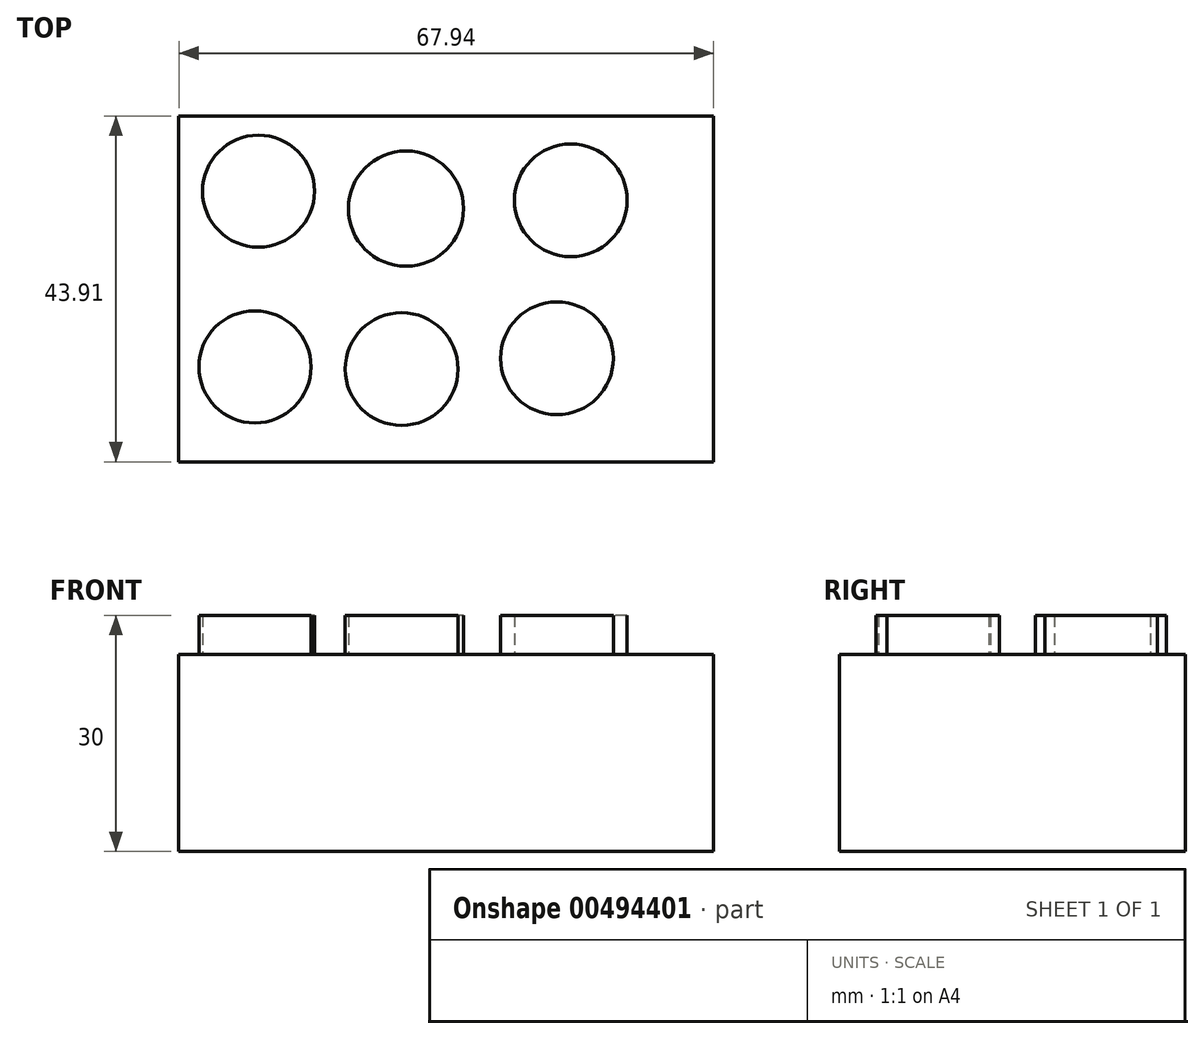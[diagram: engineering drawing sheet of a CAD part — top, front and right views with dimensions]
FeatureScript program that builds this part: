
annotation { "Feature Type Name" : "Feature", "Feature Type Description" : "" }
export const myFeature = defineFeature(function(context is Context, id is Id, definition is map)
    precondition{}
    {
        {
            var Q0;
            Q0=qCreatedBy(makeId("Top.planeOp"),FACE);
            var sketch = newSketch(context, id + "F0", { "sketchPlane" : qUnion([Q0])});
            skLineSegment(sketch, "E0.bottom", {"start": v(-65.61, 41.66) * mm, "end": v(2.33, 41.66) * mm});
            skLineSegment(sketch, "E0.top", {"start": v(-65.61, -2.25) * mm, "end": v(2.33, -2.25) * mm});
            skLineSegment(sketch, "E0.left", {"start": v(-65.61, 41.66) * mm, "end": v(-65.61, -2.25) * mm});
            skLineSegment(sketch, "E0.right", {"start": v(2.33, 41.66) * mm, "end": v(2.33, -2.25) * mm});
            skSolve(sketch);
        }
        {
            var Q0;
            Q0 = qSketchRegion(id + "F0", true);
            extrude(context, id + "F1", {"entities" : qUnion([Q0]), "depth" : 25 * mm});
        }
        {
            var Q0;
            Q0=makeQuery(id+"F1.opExtrude","CAP_FACE",FACE,{"disambiguationData":[OSD([sQuery(id+"F0.wireOp",EDGE,"E0.bottom"),sQuery(id+"F0.wireOp",EDGE,"E0.top"),sQuery(id+"F0.wireOp",EDGE,"E0.left"),sQuery(id+"F0.wireOp",EDGE,"E0.right")])],"isStart":false});
            var sketch = newSketch(context, id + "F2", { "sketchPlane" : qUnion([Q0])});
            skCircle(sketch, "E1", {"center": v(-55.95, 9.8) * mm, "radius": 7.13 * mm});
            skSolve(sketch);
        }
        {
            var Q0;
            Q0=makeQuery(id+"F2.imprint","IMPRINT",FACE,{"disambiguationData":[TD([[makeQuery(id+"F2.imprint","IMPRINT",EDGE,{"derivedFrom":sQuery(id+"F2.wireOp",EDGE,"E1")}),-1.0]])]});
            var sketch = newSketch(context, id + "F3", { "sketchPlane" : qUnion([Q0])});
            skCircle(sketch, "E2", {"center": v(-37.31, 9.53) * mm, "radius": 7.16 * mm});
            skSolve(sketch);
        }
        {
            var Q0;
            Q0=makeQuery(id+"F2.imprint","IMPRINT",FACE,{"disambiguationData":[TD([[makeQuery(id+"F2.imprint","IMPRINT",EDGE,{"derivedFrom":sQuery(id+"F2.wireOp",EDGE,"E1")}),-1.0]])]});
            var sketch = newSketch(context, id + "F4", { "sketchPlane" : qUnion([Q0])});
            skCircle(sketch, "E3", {"center": v(-17.58, 10.9) * mm, "radius": 7.16 * mm});
            skSolve(sketch);
        }
        {
            var Q0;
            Q0 = qSketchRegion(id + "F4", true);
            extrude(context, id + "F5", {"entities" : qUnion([Q0]), "operationType" : NewBodyOperationType.ADD, "depth" : 5 * mm});
        }
        {
            var Q0;
            Q0=makeQuery(id+"F2.imprint","IMPRINT",FACE,{"disambiguationData":[TD([[makeQuery(id+"F2.imprint","IMPRINT",EDGE,{"derivedFrom":sQuery(id+"F2.wireOp",EDGE,"E1")}),1.0]])]});
            extrude(context, id + "F6", {"entities" : qUnion([Q0]), "operationType" : NewBodyOperationType.ADD, "depth" : 5 * mm});
        }
        {
            var Q0;
            Q0 = qSketchRegion(id + "F3", true);
            extrude(context, id + "F7", {"entities" : qUnion([Q0]), "operationType" : NewBodyOperationType.ADD, "depth" : 5 * mm});
        }
        {
            var Q0;
            Q0=makeQuery(id+"F1.opExtrude","CAP_FACE",FACE,{"disambiguationData":[OSD([sQuery(id+"F0.wireOp",EDGE,"E0.bottom"),sQuery(id+"F0.wireOp",EDGE,"E0.top"),sQuery(id+"F0.wireOp",EDGE,"E0.left"),sQuery(id+"F0.wireOp",EDGE,"E0.right")])],"isStart":false});
            var sketch = newSketch(context, id + "F8", { "sketchPlane" : qUnion([Q0])});
            skCircle(sketch, "E4", {"center": v(-55.5, 32.13) * mm, "radius": 7.11 * mm});
            skSolve(sketch);
        }
        {
            var Q0;
            Q0=makeQuery(id+"F8.imprint","IMPRINT",FACE,{"disambiguationData":[TD([[makeQuery(id+"F8.imprint","IMPRINT",EDGE,{"derivedFrom":sQuery(id+"F8.wireOp",EDGE,"E4")}),-1.0]])]});
            var sketch = newSketch(context, id + "F9", { "sketchPlane" : qUnion([Q0])});
            skCircle(sketch, "E5", {"center": v(-36.76, 29.9) * mm, "radius": 7.32 * mm});
            skSolve(sketch);
        }
        {
            var Q0;
            Q0=makeQuery(id+"F9.imprint","IMPRINT",FACE,{"disambiguationData":[TD([[makeQuery(id+"F9.imprint","IMPRINT",EDGE,{"derivedFrom":sQuery(id+"F9.wireOp",EDGE,"E5")}),-1.0]])]});
            var sketch = newSketch(context, id + "F10", { "sketchPlane" : qUnion([Q0])});
            skCircle(sketch, "E6", {"center": v(-15.82, 30.96) * mm, "radius": 7.16 * mm});
            skSolve(sketch);
        }
        {
            var Q0;
            Q0=makeQuery(id+"F8.imprint","IMPRINT",FACE,{"disambiguationData":[TD([[makeQuery(id+"F8.imprint","IMPRINT",EDGE,{"derivedFrom":sQuery(id+"F8.wireOp",EDGE,"E4")}),1.0]])]});
            extrude(context, id + "F11", {"entities" : qUnion([Q0]), "operationType" : NewBodyOperationType.ADD, "depth" : 5 * mm});
        }
        {
            var Q0;
            Q0=makeQuery(id+"F9.imprint","IMPRINT",FACE,{"disambiguationData":[TD([[makeQuery(id+"F9.imprint","IMPRINT",EDGE,{"derivedFrom":sQuery(id+"F9.wireOp",EDGE,"E5")}),1.0]])]});
            var Q1;
            Q1=makeQuery(id+"F10.imprint","IMPRINT",FACE,{"disambiguationData":[TD([[makeQuery(id+"F10.imprint","IMPRINT",EDGE,{"derivedFrom":sQuery(id+"F10.wireOp",EDGE,"E6")}),1.0]])]});
            extrude(context, id + "F12", {"entities" : qUnion([Q0, Q1]), "operationType" : NewBodyOperationType.ADD, "depth" : 5 * mm});
        }
    });
